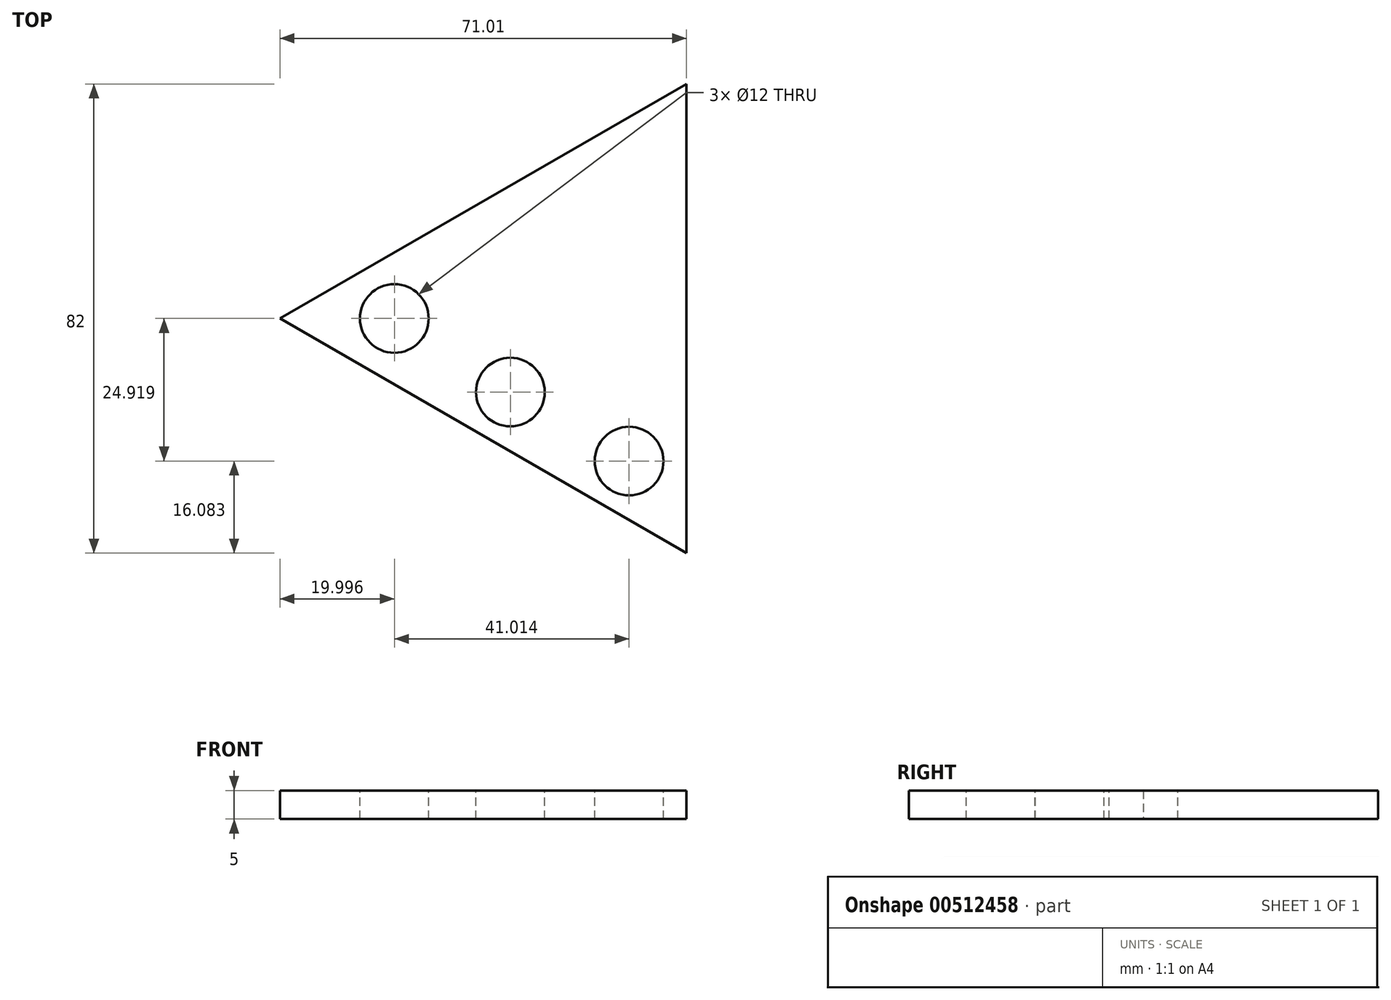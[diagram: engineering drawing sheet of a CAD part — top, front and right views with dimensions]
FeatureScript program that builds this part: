
annotation { "Feature Type Name" : "Feature", "Feature Type Description" : "" }
export const myFeature = defineFeature(function(context is Context, id is Id, definition is map)
    precondition{}
    {
        {
            var Q0;
            Q0=qCreatedBy(makeId("Top.planeOp"),FACE);
            var sketch = newSketch(context, id + "F0", { "sketchPlane" : qUnion([Q0])});
            skLineSegment(sketch, "E0", {"start": v(0, 19.63) * mm, "end": v(-71.01, -21.37) * mm});
            skLineSegment(sketch, "E1", {"start": v(-71.01, -21.37) * mm, "end": v(0, -62.37) * mm});
            skLineSegment(sketch, "E2", {"start": v(0, -62.37) * mm, "end": v(0, 19.63) * mm});
            skSolve(sketch);
        }
        {
            var Q0;
            Q0=makeQuery(id+"F0.imprint","IMPRINT",FACE,{"disambiguationData":[TD([[makeQuery(id+"F0.imprint","IMPRINT",EDGE,{"derivedFrom":sQuery(id+"F0.wireOp",EDGE,"E0")}),1.0]])]});
            extrude(context, id + "F1", {"entities" : qUnion([Q0]), "depth" : 5 * mm});
        }
        {
            var Q0;
            Q0=makeQuery(id+"F1.opExtrude","CAP_FACE",FACE,{"disambiguationData":[OSD([sQuery(id+"F0.wireOp",EDGE,"E0"),sQuery(id+"F0.wireOp",EDGE,"E1"),sQuery(id+"F0.wireOp",EDGE,"E2")])],"isStart":false});
            var sketch = newSketch(context, id + "F2", { "sketchPlane" : qUnion([Q0])});
            skCircle(sketch, "E3", {"center": v(-30.75, -34.23) * mm, "radius": 6 * mm});
            skCircle(sketch, "E4", {"center": v(-51.01, -21.37) * mm, "radius": 6 * mm});
            skCircle(sketch, "E5", {"center": v(-10, -46.29) * mm, "radius": 6 * mm});
            skSolve(sketch);
        }
        {
            var Q0;
            Q0=makeQuery(id+"F2.imprint","IMPRINT",FACE,{"disambiguationData":[TD([[makeQuery(id+"F2.imprint","IMPRINT",EDGE,{"derivedFrom":sQuery(id+"F2.wireOp",EDGE,"E4")}),1.0]])]});
            var Q1;
            Q1=makeQuery(id+"F2.imprint","IMPRINT",FACE,{"disambiguationData":[TD([[makeQuery(id+"F2.imprint","IMPRINT",EDGE,{"derivedFrom":sQuery(id+"F2.wireOp",EDGE,"E3")}),1.0]])]});
            var Q2;
            Q2=makeQuery(id+"F2.imprint","IMPRINT",FACE,{"disambiguationData":[TD([[makeQuery(id+"F2.imprint","IMPRINT",EDGE,{"derivedFrom":sQuery(id+"F2.wireOp",EDGE,"E5")}),1.0]])]});
            extrude(context, id + "F3", {"entities" : qUnion([Q0, Q1, Q2]), "operationType" : NewBodyOperationType.REMOVE, "endBound" : BoundingType.UP_TO_NEXT, "oppositeDirection" : true, "depth" : 25 * mm});
        }
    });
